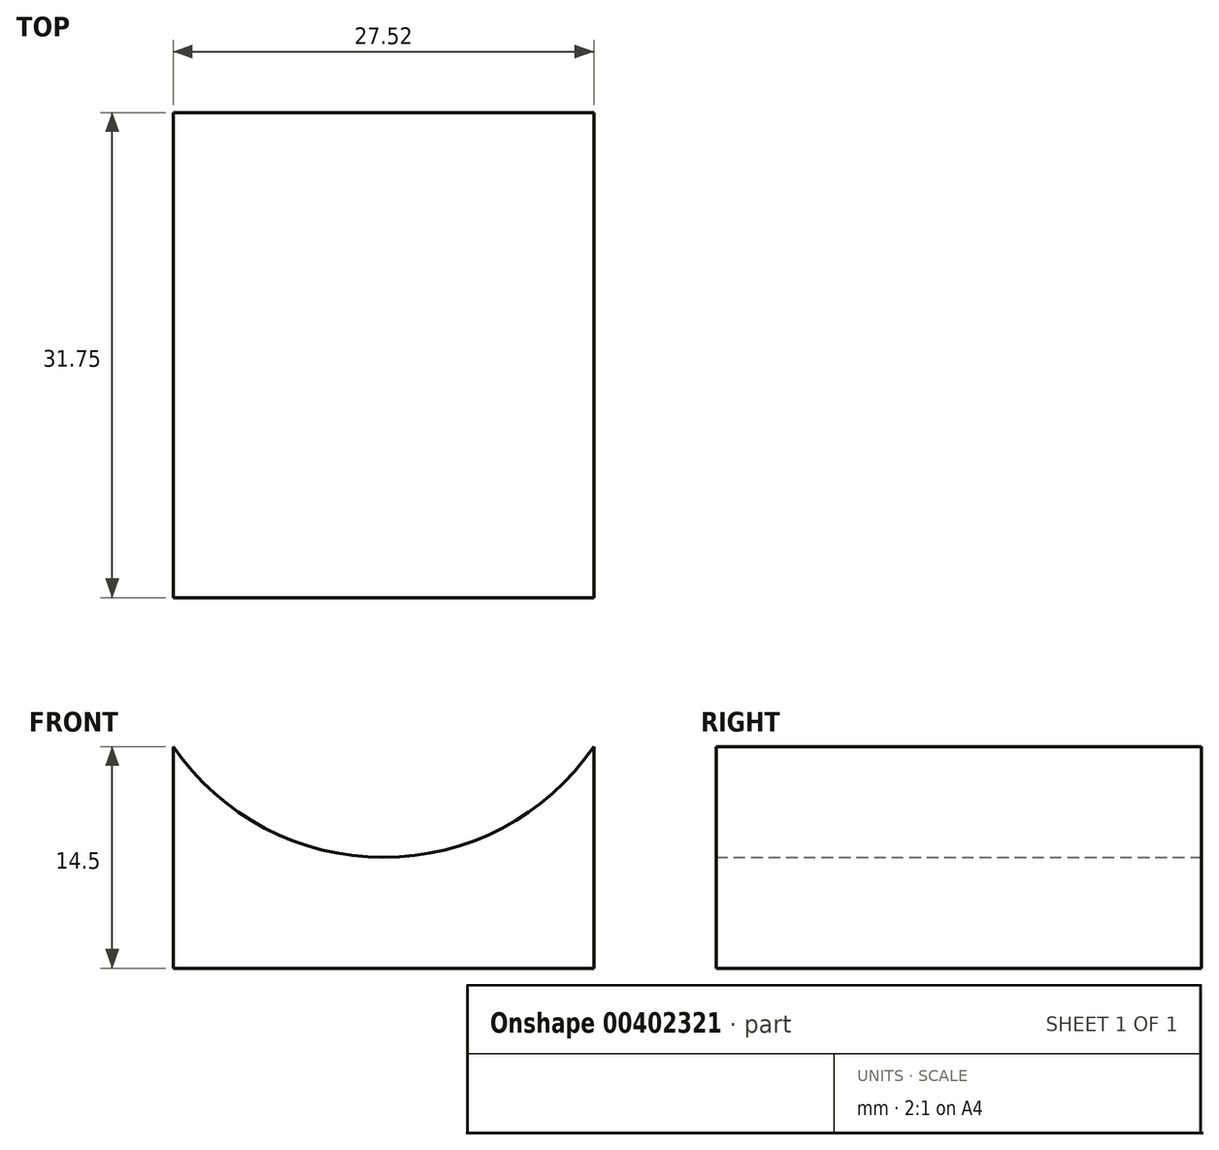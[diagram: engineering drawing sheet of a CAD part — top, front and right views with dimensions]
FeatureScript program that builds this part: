
annotation { "Feature Type Name" : "Feature", "Feature Type Description" : "" }
export const myFeature = defineFeature(function(context is Context, id is Id, definition is map)
    precondition{}
    {
        {
            var Q0;
            Q0=qCreatedBy(makeId("Front.planeOp"),FACE);
            var sketch = newSketch(context, id + "F0", { "sketchPlane" : qUnion([Q0])});
            skLineSegment(sketch, "E0.top", {"start": v(-13.76, -7.25) * mm, "end": v(13.76, -7.25) * mm});
            skLineSegment(sketch, "E0.left", {"start": v(-13.76, 7.25) * mm, "end": v(-13.76, -7.25) * mm});
            skLineSegment(sketch, "E0.right", {"start": v(13.76, 7.25) * mm, "end": v(13.76, -7.25) * mm});
            skPoint(sketch, "E0.middle", {"position": v(0, 0) * mm});
            skArc(sketch, "E1", {"start": v(-13.76, 7.25) * mm, "mid": v(0, 0) * mm, "end": v(13.76, 7.25) * mm});
            skSolve(sketch);
        }
        {
            var Q0;
            Q0 = qSketchRegion(id + "F0", true);
            extrude(context, id + "F1", {"entities" : qUnion([Q0]), "depth" : 31.75 * mm});
        }
    });
